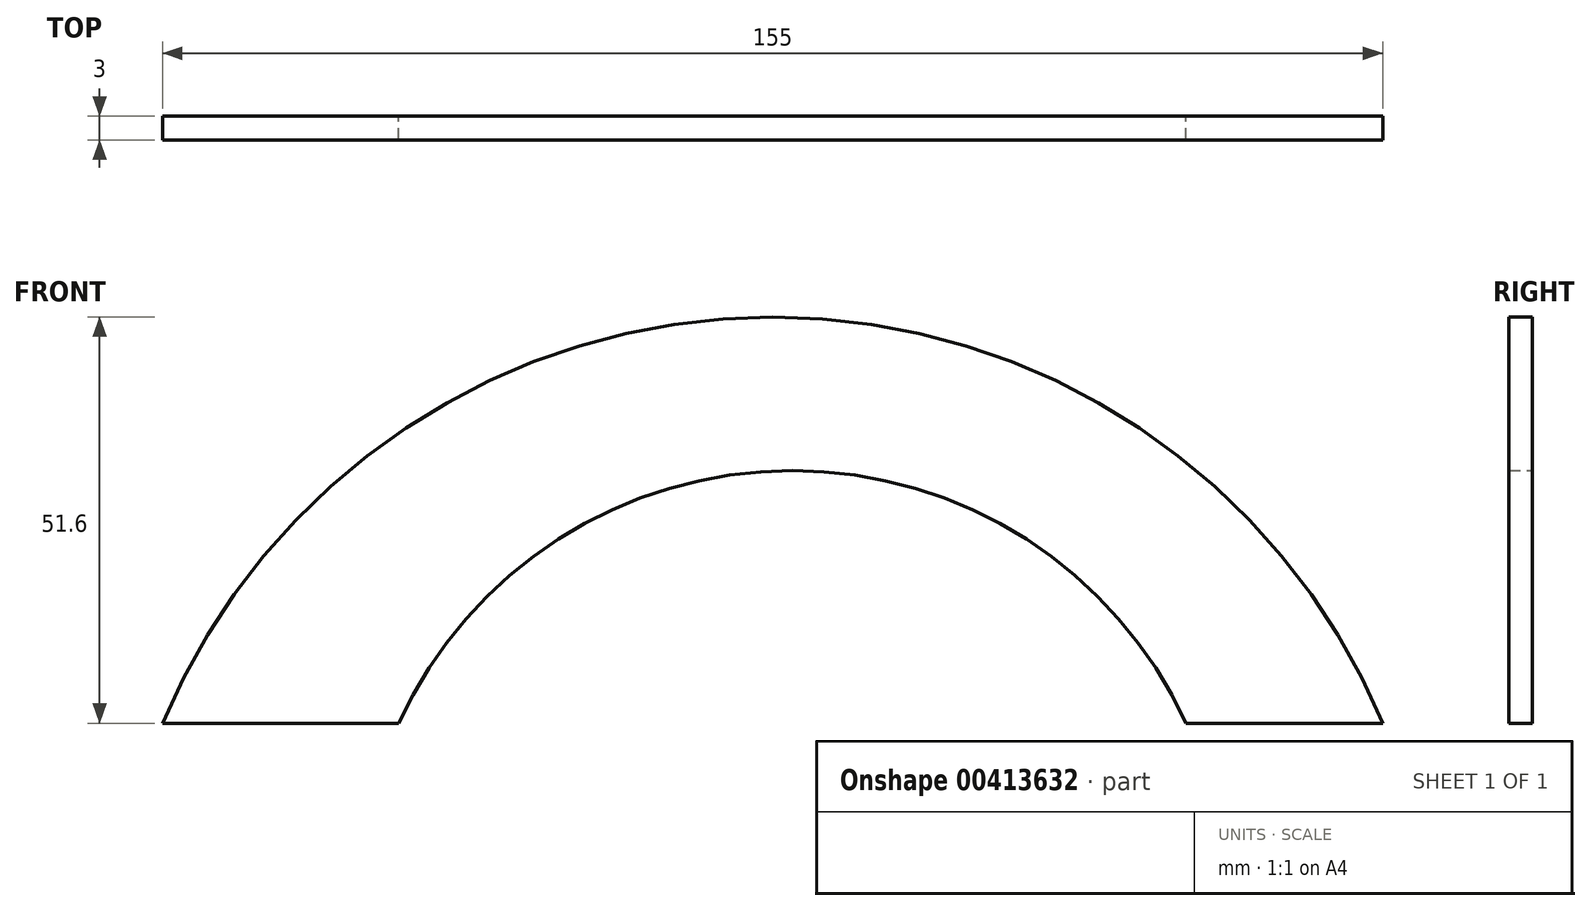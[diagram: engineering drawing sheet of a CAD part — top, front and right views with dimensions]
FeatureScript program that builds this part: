
annotation { "Feature Type Name" : "Feature", "Feature Type Description" : "" }
export const myFeature = defineFeature(function(context is Context, id is Id, definition is map)
    precondition{}
    {
        {
            var Q0;
            Q0=qCreatedBy(makeId("Front.planeOp"),FACE);
            var sketch = newSketch(context, id + "F0", { "sketchPlane" : qUnion([Q0])});
            skLineSegment(sketch, "E0", {"start": v(0, 0) * mm, "end": v(-30, 0) * mm});
            skPoint(sketch, "E1", {"position": v(0, 0) * mm});
            skPoint(sketch, "E2", {"position": v(100, 0) * mm});
            skPoint(sketch, "E3", {"position": v(125, 0) * mm});
            skLineSegment(sketch, "E4", {"start": v(100, 0) * mm, "end": v(125, 0) * mm});
            skArc(sketch, "E5", {"start": v(100, 0) * mm, "mid": v(50, 32.09) * mm, "end": v(0, 0) * mm});
            skArc(sketch, "E6", {"start": v(125, 0) * mm, "mid": v(47.5, 51.6) * mm, "end": v(-30, 0) * mm});
            skSolve(sketch);
        }
        {
            var Q0;
            Q0 = qSketchRegion(id + "F0", true);
            extrude(context, id + "F1", {"entities" : qUnion([Q0]), "depth" : 3 * mm});
        }
    });
